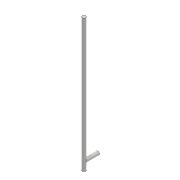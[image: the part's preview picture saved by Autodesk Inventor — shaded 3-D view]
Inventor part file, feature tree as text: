
AUTODESK INVENTOR PART (.ipt)
format: ipt  version: 2017 (Build 210142000, 142)  size: 72,704 bytes
history: native  units: mm
features: extrude x2, sketch x2
ambient origin geometry x8: Origin, YZ Plane, XZ Plane, XY Plane, X Axis, Y Axis, Z Axis, Center Point
bodies: Solid1 (feature_tree)
feature tree (4):
  extrude  "Extrusion1"  Depth=385.0mm TaperAngle=0.0deg
  extrude  "Extrusion2"  [1 undecoded]
  sketch  "Sketch1"  dims[d0=10.0mm d1=385.0mm d2=0.0mm]
  sketch  "Sketch2"  dims[d3=40.0mm d4=0.0mm]
note: 1 required parameter value undecoded (feature->parameter linkage not recoverable at this tier; creation-order binding heuristic only, values carry confidence <= 0.55)
